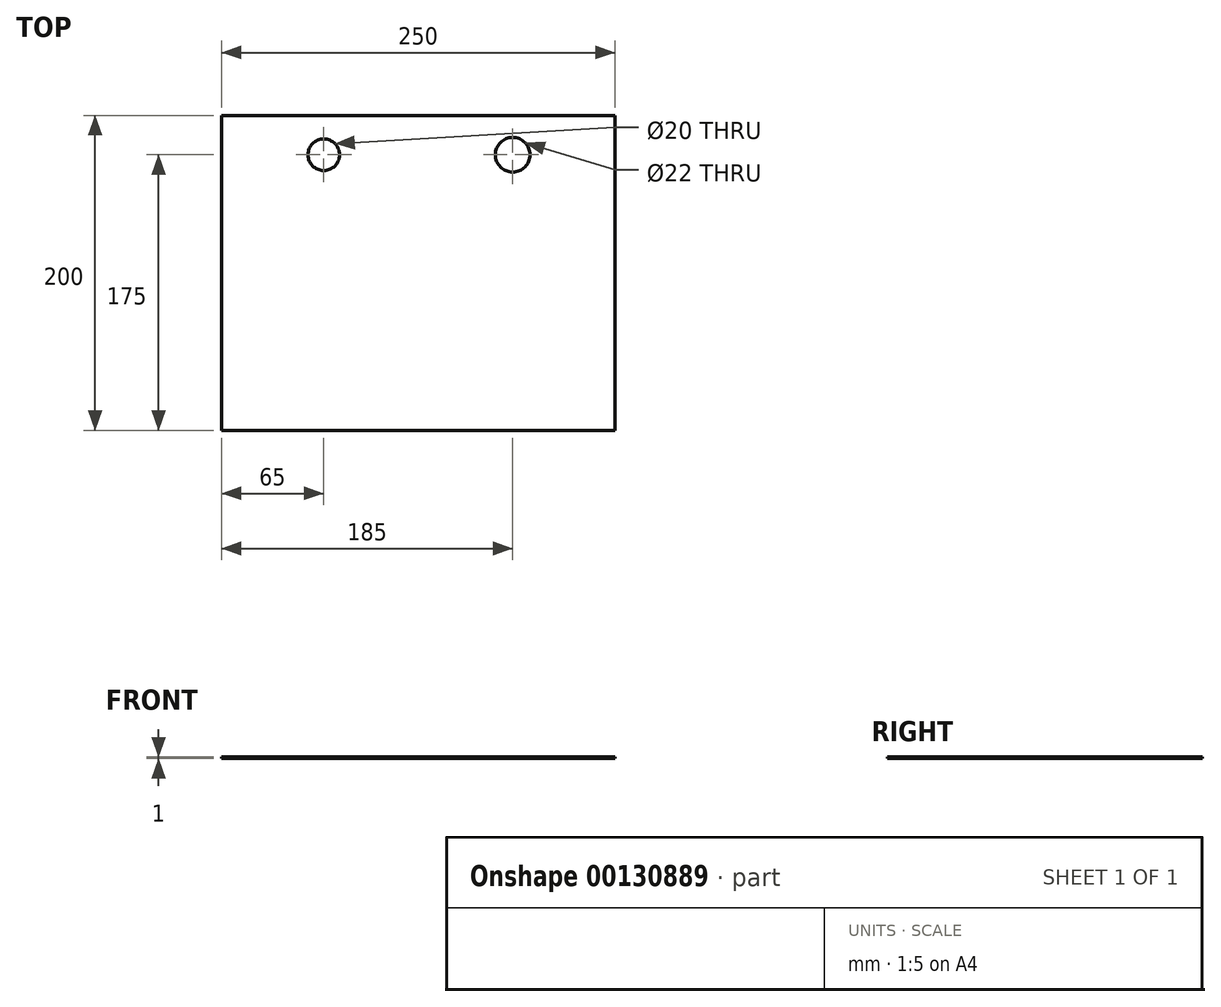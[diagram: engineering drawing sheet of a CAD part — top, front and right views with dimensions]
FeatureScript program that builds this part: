
annotation { "Feature Type Name" : "Feature", "Feature Type Description" : "" }
export const myFeature = defineFeature(function(context is Context, id is Id, definition is map)
    precondition{}
    {
        {
            var Q0;
            Q0=qCreatedBy(makeId("Top.planeOp"),FACE);
            var sketch = newSketch(context, id + "F0", { "sketchPlane" : qUnion([Q0])});
            skLineSegment(sketch, "E0.bottom", {"start": v(0, 0) * mm, "end": v(250, 0) * mm});
            skLineSegment(sketch, "E0.top", {"start": v(0, 200) * mm, "end": v(250, 200) * mm});
            skLineSegment(sketch, "E0.left", {"start": v(0, 0) * mm, "end": v(0, 200) * mm});
            skLineSegment(sketch, "E0.right", {"start": v(250, 0) * mm, "end": v(250, 200) * mm});
            skLineSegment(sketch, "E1.bottom", {"start": v(0, 200) * mm, "end": v(0, 200) * mm});
            skLineSegment(sketch, "E2", {"start": v(0, 200) * mm, "end": v(65, 200) * mm});
            skLineSegment(sketch, "E3", {"start": v(250, 200) * mm, "end": v(185, 200) * mm});
            skCircle(sketch, "E4", {"center": v(65, 175) * mm, "radius": 10 * mm});
            skCircle(sketch, "E5", {"center": v(185, 175) * mm, "radius": 11 * mm});
            skSolve(sketch);
        }
        {
            var Q0;
            Q0 = qSketchRegion(id + "F0", true);
            extrude(context, id + "F1", {"entities" : qUnion([Q0]), "depth" : 1 * mm});
        }
    });
